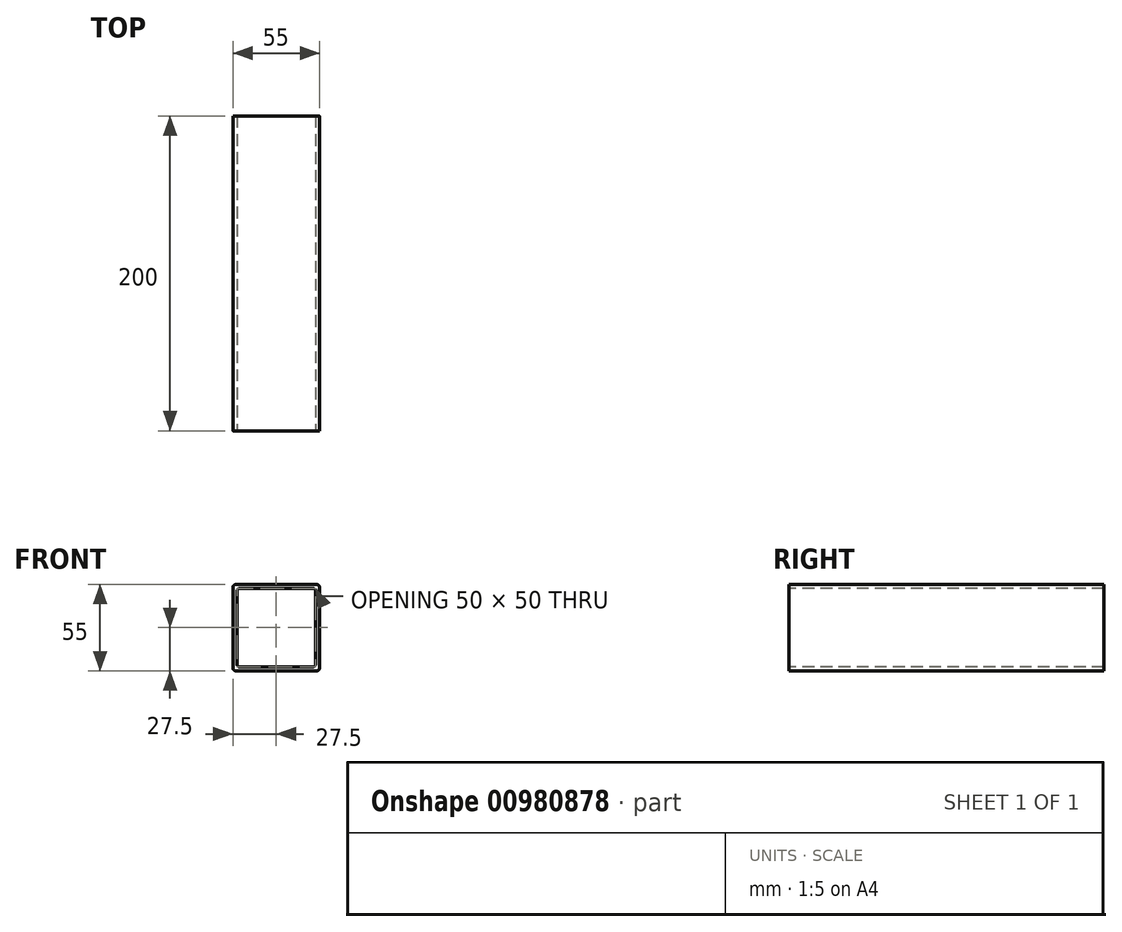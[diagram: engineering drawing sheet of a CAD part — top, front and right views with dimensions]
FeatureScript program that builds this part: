
annotation { "Feature Type Name" : "Feature", "Feature Type Description" : "" }
export const myFeature = defineFeature(function(context is Context, id is Id, definition is map)
    precondition{}
    {
        {
            var Q0;
            Q0=qCreatedBy(makeId("Front.planeOp"),FACE);
            var sketch = newSketch(context, id + "F0", { "sketchPlane" : qUnion([Q0])});
            skLineSegment(sketch, "E0.bottom", {"start": v(25.5, 27.5) * mm, "end": v(-25.5, 27.5) * mm});
            skLineSegment(sketch, "E0.top", {"start": v(25.5, -27.5) * mm, "end": v(-25.5, -27.5) * mm});
            skLineSegment(sketch, "E0.left", {"start": v(27.5, 25.5) * mm, "end": v(27.5, -25.5) * mm});
            skLineSegment(sketch, "E0.right", {"start": v(-27.5, 25.5) * mm, "end": v(-27.5, -25.5) * mm});
            skPoint(sketch, "E0.middle", {"position": v(0, 0) * mm});
            skLineSegment(sketch, "E1.bottom", {"start": v(23, 25) * mm, "end": v(-23, 25) * mm});
            skLineSegment(sketch, "E1.top", {"start": v(23, -25) * mm, "end": v(-23, -25) * mm});
            skLineSegment(sketch, "E1.left", {"start": v(25, 23) * mm, "end": v(25, -23) * mm});
            skLineSegment(sketch, "E1.right", {"start": v(-25, 23) * mm, "end": v(-25, -23) * mm});
            skPoint(sketch, "E2.visualSharp", {"position": v(27.5, 27.5) * mm});
            skArc(sketch, "E2.filletArc", {"start": v(27.5, 25.5) * mm, "mid": v(26.91, 26.91) * mm, "end": v(25.5, 27.5) * mm});
            skPoint(sketch, "E3.visualSharp", {"position": v(25, 25) * mm});
            skArc(sketch, "E3.filletArc", {"start": v(25, 23) * mm, "mid": v(24.41, 24.41) * mm, "end": v(23, 25) * mm});
            skPoint(sketch, "E4.visualSharp", {"position": v(27.5, -27.5) * mm});
            skArc(sketch, "E4.filletArc", {"start": v(25.5, -27.5) * mm, "mid": v(26.91, -26.91) * mm, "end": v(27.5, -25.5) * mm});
            skPoint(sketch, "E5.visualSharp", {"position": v(25, -25) * mm});
            skArc(sketch, "E5.filletArc", {"start": v(23, -25) * mm, "mid": v(24.41, -24.41) * mm, "end": v(25, -23) * mm});
            skPoint(sketch, "E6.visualSharp", {"position": v(-25, -25) * mm});
            skArc(sketch, "E6.filletArc", {"start": v(-25, -23) * mm, "mid": v(-24.41, -24.41) * mm, "end": v(-23, -25) * mm});
            skPoint(sketch, "E7.visualSharp", {"position": v(-27.5, -27.5) * mm});
            skArc(sketch, "E7.filletArc", {"start": v(-27.5, -25.5) * mm, "mid": v(-26.91, -26.91) * mm, "end": v(-25.5, -27.5) * mm});
            skPoint(sketch, "E8.visualSharp", {"position": v(-27.5, 27.5) * mm});
            skArc(sketch, "E8.filletArc", {"start": v(-25.5, 27.5) * mm, "mid": v(-26.91, 26.91) * mm, "end": v(-27.5, 25.5) * mm});
            skPoint(sketch, "E9.visualSharp", {"position": v(-25, 25) * mm});
            skArc(sketch, "E9.filletArc", {"start": v(-23, 25) * mm, "mid": v(-24.41, 24.41) * mm, "end": v(-25, 23) * mm});
            skSolve(sketch);
        }
        {
            var Q0;
            Q0=makeQuery(id+"F0.imprint","IMPRINT",FACE,{"disambiguationData":[TD([[makeQuery(id+"F0.imprint","IMPRINT",EDGE,{"derivedFrom":sQuery(id+"F0.wireOp",EDGE,"E0.bottom")}),1.0]])]});
            extrude(context, id + "F1", {"entities" : qUnion([Q0]), "oppositeDirection" : true, "depth" : 200 * mm, "offsetDistance" : 25 * mm});
        }
    });
